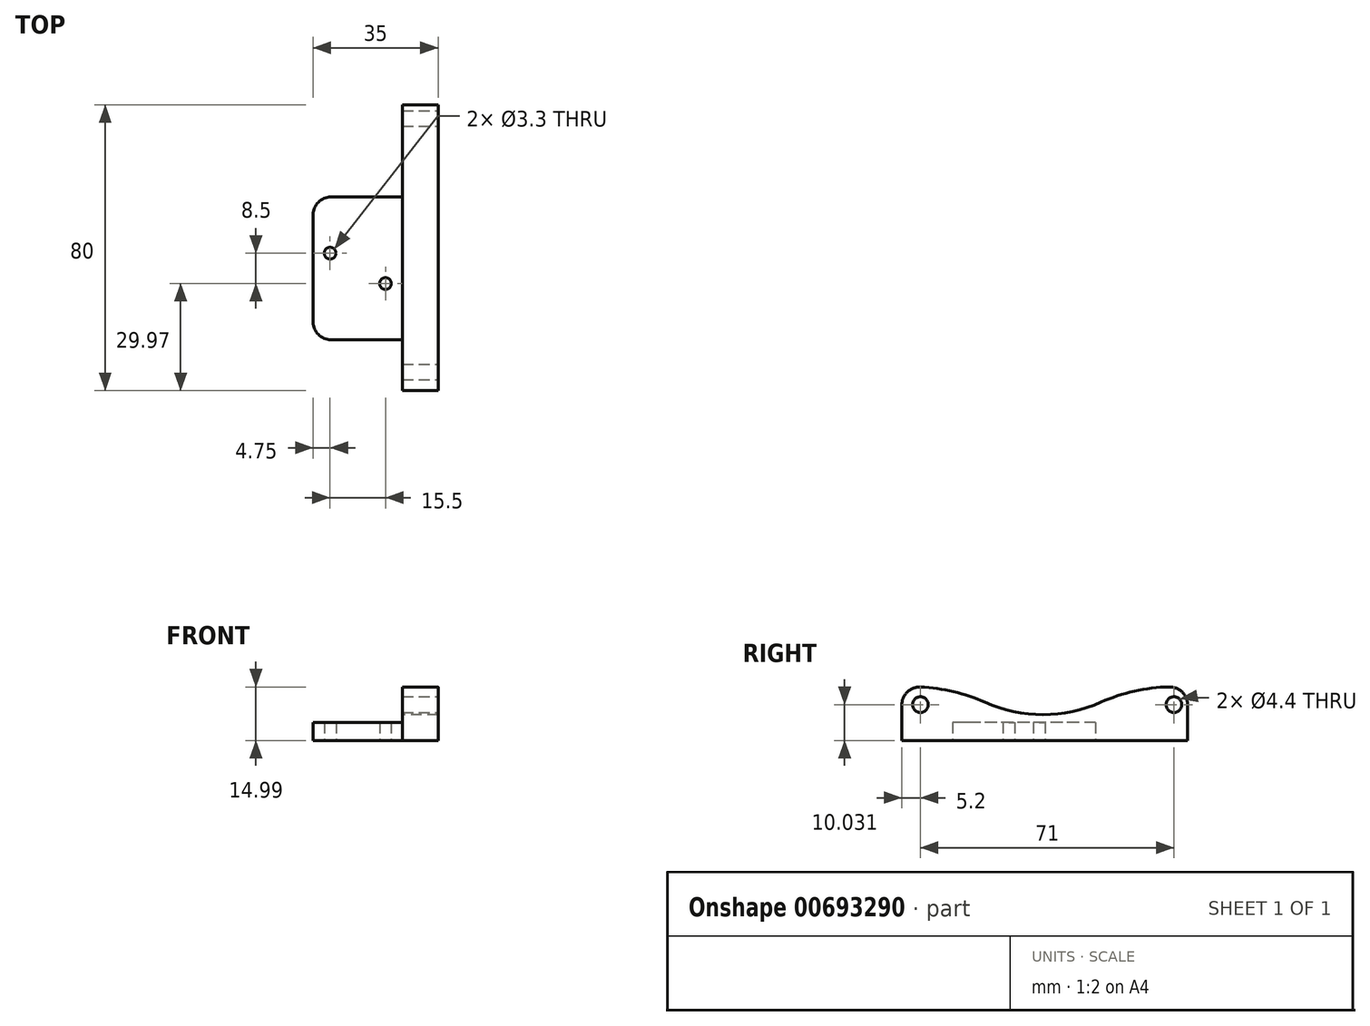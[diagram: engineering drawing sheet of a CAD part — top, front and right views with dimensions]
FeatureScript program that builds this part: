
annotation { "Feature Type Name" : "Feature", "Feature Type Description" : "" }
export const myFeature = defineFeature(function(context is Context, id is Id, definition is map)
    precondition{}
    {
        {
            var Q0;
            Q0=qCreatedBy(makeId("Top.planeOp"),FACE);
            var sketch = newSketch(context, id + "F0", { "sketchPlane" : qUnion([Q0])});
            skLineSegment(sketch, "E0.bottom", {"start": v(7.75, 4.25) * mm, "end": v(-7.75, 4.25) * mm, "construction": true});
            skLineSegment(sketch, "E0.top", {"start": v(7.75, -4.25) * mm, "end": v(-7.75, -4.25) * mm, "construction": true});
            skLineSegment(sketch, "E0.left", {"start": v(7.75, 4.25) * mm, "end": v(7.75, -4.25) * mm, "construction": true});
            skLineSegment(sketch, "E0.right", {"start": v(-7.75, 4.25) * mm, "end": v(-7.75, -4.25) * mm, "construction": true});
            skPoint(sketch, "E0.middle", {"position": v(0, 0) * mm});
            skLineSegment(sketch, "E1.bottom", {"start": v(12.5, 20) * mm, "end": v(-12.5, 20) * mm});
            skLineSegment(sketch, "E1.top", {"start": v(12.5, -20) * mm, "end": v(-12.5, -20) * mm});
            skLineSegment(sketch, "E1.left", {"start": v(12.5, 20) * mm, "end": v(12.5, -20) * mm});
            skLineSegment(sketch, "E1.right", {"start": v(-12.5, 20) * mm, "end": v(-12.5, -20) * mm});
            skLineSegment(sketch, "E2", {"start": v(12.5, 20) * mm, "end": v(12.5, 45.78) * mm});
            skLineSegment(sketch, "E3", {"start": v(12.5, 45.78) * mm, "end": v(22.5, 45.78) * mm});
            skLineSegment(sketch, "E4", {"start": v(22.5, 45.78) * mm, "end": v(22.5, -34.22) * mm});
            skLineSegment(sketch, "E5", {"start": v(22.5, -34.22) * mm, "end": v(12.5, -34.22) * mm});
            skLineSegment(sketch, "E6", {"start": v(12.5, -34.22) * mm, "end": v(12.5, -20) * mm});
            skSolve(sketch);
        }
        {
            var Q0;
            Q0=makeQuery(id+"F0.imprint","IMPRINT",FACE,{"disambiguationData":[TD([[makeQuery(id+"F0.imprint","IMPRINT",EDGE,{"derivedFrom":sQuery(id+"F0.wireOp",EDGE,"E1.bottom")}),1.0]])]});
            extrude(context, id + "F1", {"entities" : qUnion([Q0]), "depth" : 5 * mm, "offsetDistance" : 25 * mm});
        }
        {
            var Q0;
            Q0=sQuery(id+"F0.wireOp",VERTEX,"E0.right.start");
            var Q1;
            Q1=sQuery(id+"F0.wireOp",VERTEX,"E0.left.end");
            var Q2;
            Q2=makeQuery(id+"F1.opExtrude","SWEPT_BODY",BODY,{"disambiguationData":[OSD([sQuery(id+"F0.wireOp",EDGE,"E1.bottom"),sQuery(id+"F0.wireOp",EDGE,"E1.top"),sQuery(id+"F0.wireOp",EDGE,"E1.left"),sQuery(id+"F0.wireOp",EDGE,"E1.right")])]});
            hole(context, id + "F2", {"style" : HoleStyle.SIMPLE, "endStyle" : HoleEndStyle.THROUGH, "oppositeDirection" : true, "standardTappedOrClearance" : lookupTablePath({ "standard" : "ISO", "fit" : "Normal", "size" : "M3", "type" : "Clearance" }), "standardBlindInLast" : lookupTablePath({ "fit" : "Standard", "standard" : "ISO", "size" : "M3", "type" : "Clearance" }), "holeDiameter" : 3.3 * mm, "majorDiameter" : 5 * mm, "isTappedThrough" : true, "tappedDepth" : 12 * mm, "tapClearance" : 3, "startFromSketch" : true, "locations" : qUnion([Q0, Q1]), "scope" : qUnion([Q2])});
        }
        {
            var Q0;
            Q0=makeQuery(id+"F0.imprint","IMPRINT",FACE,{"disambiguationData":[TD([[makeQuery(id+"F0.imprint","IMPRINT",EDGE,{"derivedFrom":sQuery(id+"F0.wireOp",EDGE,"E1.left")}),1.0]])]});
            extrude(context, id + "F3", {"entities" : qUnion([Q0]), "operationType" : NewBodyOperationType.ADD, "depth" : 15 * mm, "offsetDistance" : 25 * mm});
        }
        {
            var Q0;
            Q0=makeQuery(id+"F3.opExtrude","SWEPT_FACE",FACE,{"disambiguationData":[OSD([sQuery(id+"F0.wireOp",EDGE,"E5")])]});
            var sketch = newSketch(context, id + "F4", { "sketchPlane" : qUnion([Q0])});
            skLineSegment(sketch, "E7", {"start": v(15.88, 16.53) * mm, "end": v(15.88, -1.5) * mm});
            skLineSegment(sketch, "E8", {"start": v(15.88, -1.5) * mm, "end": v(24.4, -1.5) * mm});
            skLineSegment(sketch, "E9", {"start": v(24.4, -1.5) * mm, "end": v(24.4, 16.53) * mm});
            skLineSegment(sketch, "E10", {"start": v(24.4, 16.53) * mm, "end": v(15.88, 16.53) * mm});
            skSolve(sketch);
        }
        {
            var Q0;
            {var subQ0=sQuery(id+"F4.wireOp",EDGE,"E8");var subQ1=sQuery(id+"F4.wireOp",EDGE,"E7");var subQ2=makeQuery(id+"F4.imprint","INTERSECT",VERTEX,{"derivedFrom":[subQ1,subQ0]});Q0=makeQuery(id+"F4.imprint","IMPRINT",FACE,{"disambiguationData":[TD([[makeQuery(id+"F4.imprint","IMPRINT",EDGE,{"disambiguationData":[TD([[subQ2,1.0]])],"derivedFrom":subQ1}),1.0]])]});}
            extrude(context, id + "F5", {"entities" : qUnion([Q0]), "operationType" : NewBodyOperationType.REMOVE, "oppositeDirection" : true, "depth" : 100 * mm, "offsetDistance" : 25 * mm});
        }
        {
            var Q0;
            Q0=qCreatedBy(makeId("Right.planeOp"),FACE);
            var sketch = newSketch(context, id + "F6", { "sketchPlane" : qUnion([Q0])});
            skCircle(sketch, "E11", {"center": v(5.3, 47.24) * mm, "radius": 40 * mm});
            skSolve(sketch);
        }
        {
            var Q0;
            Q0=makeQuery(id+"F6.imprint","IMPRINT",FACE,{"disambiguationData":[TD([[makeQuery(id+"F6.imprint","IMPRINT",EDGE,{"derivedFrom":sQuery(id+"F6.wireOp",EDGE,"E11")}),1.0]])]});
            extrude(context, id + "F7", {"entities" : qUnion([Q0]), "operationType" : NewBodyOperationType.REMOVE, "depth" : 25 * mm, "offsetDistance" : 25 * mm});
        }
        {
            var Q0;
            Q0=makeQuery(id+"F1.opExtrude","SWEPT_EDGE",EDGE,{"disambiguationData":[OSD([sQuery(id+"F0.wireOp",EDGE,"E1.top"),sQuery(id+"F0.wireOp",EDGE,"E1.left"),sQuery(id+"F0.wireOp",EDGE,"E6")])]});
            var Q1;
            Q1=makeQuery(id+"F1.opExtrude","SWEPT_EDGE",EDGE,{"disambiguationData":[OSD([sQuery(id+"F0.wireOp",EDGE,"E1.bottom"),sQuery(id+"F0.wireOp",EDGE,"E1.left"),sQuery(id+"F0.wireOp",EDGE,"E2")])]});
            var Q2;
            Q2=makeQuery(id+"F1.opExtrude","SWEPT_EDGE",EDGE,{"disambiguationData":[OSD([sQuery(id+"F0.wireOp",EDGE,"E1.bottom"),sQuery(id+"F0.wireOp",EDGE,"E1.right")])]});
            var Q3;
            Q3=makeQuery(id+"F1.opExtrude","SWEPT_EDGE",EDGE,{"disambiguationData":[OSD([sQuery(id+"F0.wireOp",EDGE,"E1.top"),sQuery(id+"F0.wireOp",EDGE,"E1.right")])]});
            fillet(context, id + "F8", {"entities" : qUnion([Q0, Q1, Q2, Q3]), "radius" : 5 * mm, "tangentPropagation" : true, "allowEdgeOverflow" : false});
        }
        {
            var Q0;
            Q0=makeQuery(id+"F7.boolean.opBoolean","INTERSECT",EDGE,{"disambiguationData":[OD(0.0)],"derivedFrom":[makeQuery(id+"F3.opExtrude","CAP_FACE",FACE,{"disambiguationData":[OSD([sQuery(id+"F0.wireOp",EDGE,"E1.left"),sQuery(id+"F0.wireOp",EDGE,"E2"),sQuery(id+"F0.wireOp",EDGE,"E3"),sQuery(id+"F0.wireOp",EDGE,"E4"),sQuery(id+"F0.wireOp",EDGE,"E5"),sQuery(id+"F0.wireOp",EDGE,"E6")])],"isStart":false}),makeQuery(id+"F7.opExtrude","SWEPT_FACE",FACE,{"disambiguationData":[OSD([sQuery(id+"F6.wireOp",EDGE,"E11")])]})]});
            var Q1;
            Q1=makeQuery(id+"F7.boolean.opBoolean","INTERSECT",EDGE,{"disambiguationData":[OD(1.0)],"derivedFrom":[makeQuery(id+"F3.opExtrude","CAP_FACE",FACE,{"disambiguationData":[OSD([sQuery(id+"F0.wireOp",EDGE,"E1.left"),sQuery(id+"F0.wireOp",EDGE,"E2"),sQuery(id+"F0.wireOp",EDGE,"E3"),sQuery(id+"F0.wireOp",EDGE,"E4"),sQuery(id+"F0.wireOp",EDGE,"E5"),sQuery(id+"F0.wireOp",EDGE,"E6")])],"isStart":false}),makeQuery(id+"F7.opExtrude","SWEPT_FACE",FACE,{"disambiguationData":[OSD([sQuery(id+"F6.wireOp",EDGE,"E11")])]})]});
            fillet(context, id + "F9", {"entities" : qUnion([Q0, Q1]), "radius" : 50 * mm, "tangentPropagation" : true, "allowEdgeOverflow" : false});
        }
        {
            var Q0;
            Q0=makeQuery(id+"F3.opExtrude","SWEPT_FACE",FACE,{"disambiguationData":[OSD([sQuery(id+"F0.wireOp",EDGE,"E4")])]});
            var sketch = newSketch(context, id + "F10", { "sketchPlane" : qUnion([Q0])});
            skLineSegment(sketch, "E12", {"start": v(-29.02, 10.03) * mm, "end": v(41.98, 10.03) * mm, "construction": true});
            skSolve(sketch);
        }
        {
            var Q0;
            Q0=sQuery(id+"F10.wireOp",VERTEX,"E12.start");
            var Q1;
            Q1=sQuery(id+"F10.wireOp",VERTEX,"E12.end");
            var Q2;
            Q2=makeQuery(id+"F1.opExtrude","SWEPT_BODY",BODY,{"disambiguationData":[OSD([sQuery(id+"F0.wireOp",EDGE,"E1.bottom"),sQuery(id+"F0.wireOp",EDGE,"E1.top"),sQuery(id+"F0.wireOp",EDGE,"E1.left"),sQuery(id+"F0.wireOp",EDGE,"E1.right")])]});
            hole(context, id + "F11", {"style" : HoleStyle.SIMPLE, "endStyle" : HoleEndStyle.THROUGH, "standardTappedOrClearance" : lookupTablePath({ "standard" : "ISO", "fit" : "Normal", "size" : "M4", "type" : "Clearance" }), "standardBlindInLast" : lookupTablePath({ "fit" : "Standard", "standard" : "ISO", "size" : "M4", "type" : "Clearance" }), "holeDiameter" : 4.4 * mm, "majorDiameter" : 5 * mm, "isTappedThrough" : true, "tappedDepth" : 12 * mm, "tapClearance" : 3, "startFromSketch" : true, "locations" : qUnion([Q0, Q1]), "scope" : qUnion([Q2])});
        }
        {
            var Q0;
            Q0=makeQuery(id+"F3.opExtrude","CAP_EDGE",EDGE,{"disambiguationData":[OSD([sQuery(id+"F0.wireOp",EDGE,"E5")])],"isStart":false});
            var Q1;
            Q1=makeQuery(id+"F3.opExtrude","CAP_EDGE",EDGE,{"disambiguationData":[OSD([sQuery(id+"F0.wireOp",EDGE,"E3")])],"isStart":false});
            fillet(context, id + "F12", {"entities" : qUnion([Q0, Q1]), "radius" : 5 * mm, "tangentPropagation" : true, "allowEdgeOverflow" : false});
        }
    });
